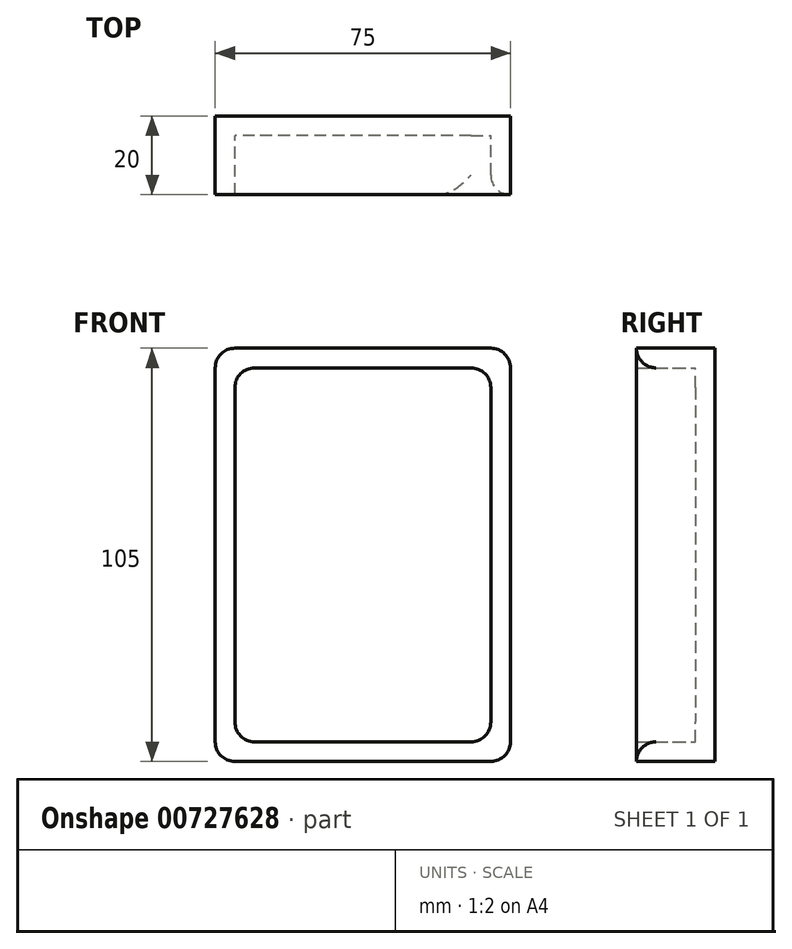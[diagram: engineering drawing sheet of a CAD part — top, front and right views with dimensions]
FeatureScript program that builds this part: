
annotation { "Feature Type Name" : "Feature", "Feature Type Description" : "" }
export const myFeature = defineFeature(function(context is Context, id is Id, definition is map)
    precondition{}
    {
        {
            var Q0;
            Q0=qCreatedBy(makeId("Front.planeOp"),FACE);
            var sketch = newSketch(context, id + "F0", { "sketchPlane" : qUnion([Q0])});
            skLineSegment(sketch, "E0.bottom", {"start": v(37.98, 53.84) * mm, "end": v(-37.02, 53.84) * mm});
            skLineSegment(sketch, "E0.top", {"start": v(37.98, -51.16) * mm, "end": v(-37.02, -51.16) * mm});
            skLineSegment(sketch, "E0.left", {"start": v(37.98, 53.84) * mm, "end": v(37.98, -51.16) * mm});
            skLineSegment(sketch, "E0.right", {"start": v(-37.02, 53.84) * mm, "end": v(-37.02, -51.16) * mm});
            skSolve(sketch);
        }
        {
            var Q0;
            Q0 = qSketchRegion(id + "F0", true);
            extrude(context, id + "F1", {"entities" : qUnion([Q0]), "depth" : 20 * mm, "offsetDistance" : 25 * mm});
        }
        {
            var Q0;
            Q0=makeQuery(id+"F1.opExtrude","CAP_FACE",FACE,{"disambiguationData":[OSD([sQuery(id+"F0.wireOp",EDGE,"E0.bottom"),sQuery(id+"F0.wireOp",EDGE,"E0.top"),sQuery(id+"F0.wireOp",EDGE,"E0.left"),sQuery(id+"F0.wireOp",EDGE,"E0.right")])],"isStart":false});
            shell(context, id + "F2", {"entities" : qUnion([Q0]), "thickness" : 5 * mm});
        }
        {
            var Q0;
            Q0=makeQuery(id+"F1.opExtrude","SWEPT_EDGE",EDGE,{"disambiguationData":[OSD([sQuery(id+"F0.wireOp",EDGE,"E0.bottom"),sQuery(id+"F0.wireOp",EDGE,"E0.right")])]});
            var Q1;
            Q1=makeQuery(id+"F1.opExtrude","SWEPT_EDGE",EDGE,{"disambiguationData":[OSD([sQuery(id+"F0.wireOp",EDGE,"E0.top"),sQuery(id+"F0.wireOp",EDGE,"E0.right")])]});
            var Q2;
            Q2=makeQuery(id+"F1.opExtrude","SWEPT_EDGE",EDGE,{"disambiguationData":[OSD([sQuery(id+"F0.wireOp",EDGE,"E0.bottom"),sQuery(id+"F0.wireOp",EDGE,"E0.left")])]});
            var Q3;
            Q3=makeQuery(id+"F1.opExtrude","SWEPT_EDGE",EDGE,{"disambiguationData":[OSD([sQuery(id+"F0.wireOp",EDGE,"E0.top"),sQuery(id+"F0.wireOp",EDGE,"E0.left")])]});
            var Q4;
            Q4=makeQuery(id+"F2.opShell","OFFSET_EDGE",EDGE,{"disambiguationData":[OSD([sQuery(id+"F0.wireOp",EDGE,"E0.bottom"),sQuery(id+"F0.wireOp",EDGE,"E0.right")])]});
            var Q5;
            Q5=makeQuery(id+"F2.opShell","OFFSET_EDGE",EDGE,{"disambiguationData":[OSD([sQuery(id+"F0.wireOp",EDGE,"E0.bottom"),sQuery(id+"F0.wireOp",EDGE,"E0.left")])]});
            var Q6;
            Q6=makeQuery(id+"F2.opShell","OFFSET_EDGE",EDGE,{"disambiguationData":[OSD([sQuery(id+"F0.wireOp",EDGE,"E0.top"),sQuery(id+"F0.wireOp",EDGE,"E0.right")])]});
            var Q7;
            Q7=makeQuery(id+"F2.opShell","OFFSET_EDGE",EDGE,{"disambiguationData":[OSD([sQuery(id+"F0.wireOp",EDGE,"E0.top"),sQuery(id+"F0.wireOp",EDGE,"E0.left")])]});
            var Q8;
            {var subQ0=sQuery(id+"F0.wireOp",EDGE,"E0.left");Q8=makeQuery(id+"F2.opShell","OFFSET_EDGE",EDGE,{"disambiguationData":[OSD([subQ0]),TDD([makeQuery(id+"F1.opExtrude","CAP_EDGE",EDGE,{"disambiguationData":[OSD([subQ0])],"isStart":false})])]});}
            fillet(context, id + "F3", {"entities" : qUnion([Q0, Q1, Q2, Q3, Q4, Q5, Q6, Q7, Q8]), "radius" : 5 * mm, "tangentPropagation" : true, "allowEdgeOverflow" : false});
        }
    });
